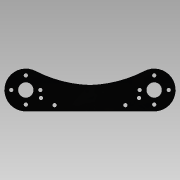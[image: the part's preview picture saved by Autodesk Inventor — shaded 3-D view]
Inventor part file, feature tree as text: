
AUTODESK INVENTOR PART (.ipt)
format: ipt  version: 2015 SP1 (Build 190203100, 203)  size: 110,592 bytes
history: native  units: mm
features: extrude x1, sketch x1
ambient origin geometry x8: Origin, YZ Plane, XZ Plane, XY Plane, X Axis, Y Axis, Z Axis, Center Point
bodies: Body1 (feature_tree)
feature tree (2):
  extrude  "Extrusion3"  Depth=3.5mm
  sketch  "Sketch1"  dims[d47=8.509mm d48=8.509mm d49=8.509mm d50=8.509mm d51=10.0mm d53=9.0mm d56=9.0mm d58=4.19811mm d61=75.0mm d62=3.5mm d63=0.0mm]
